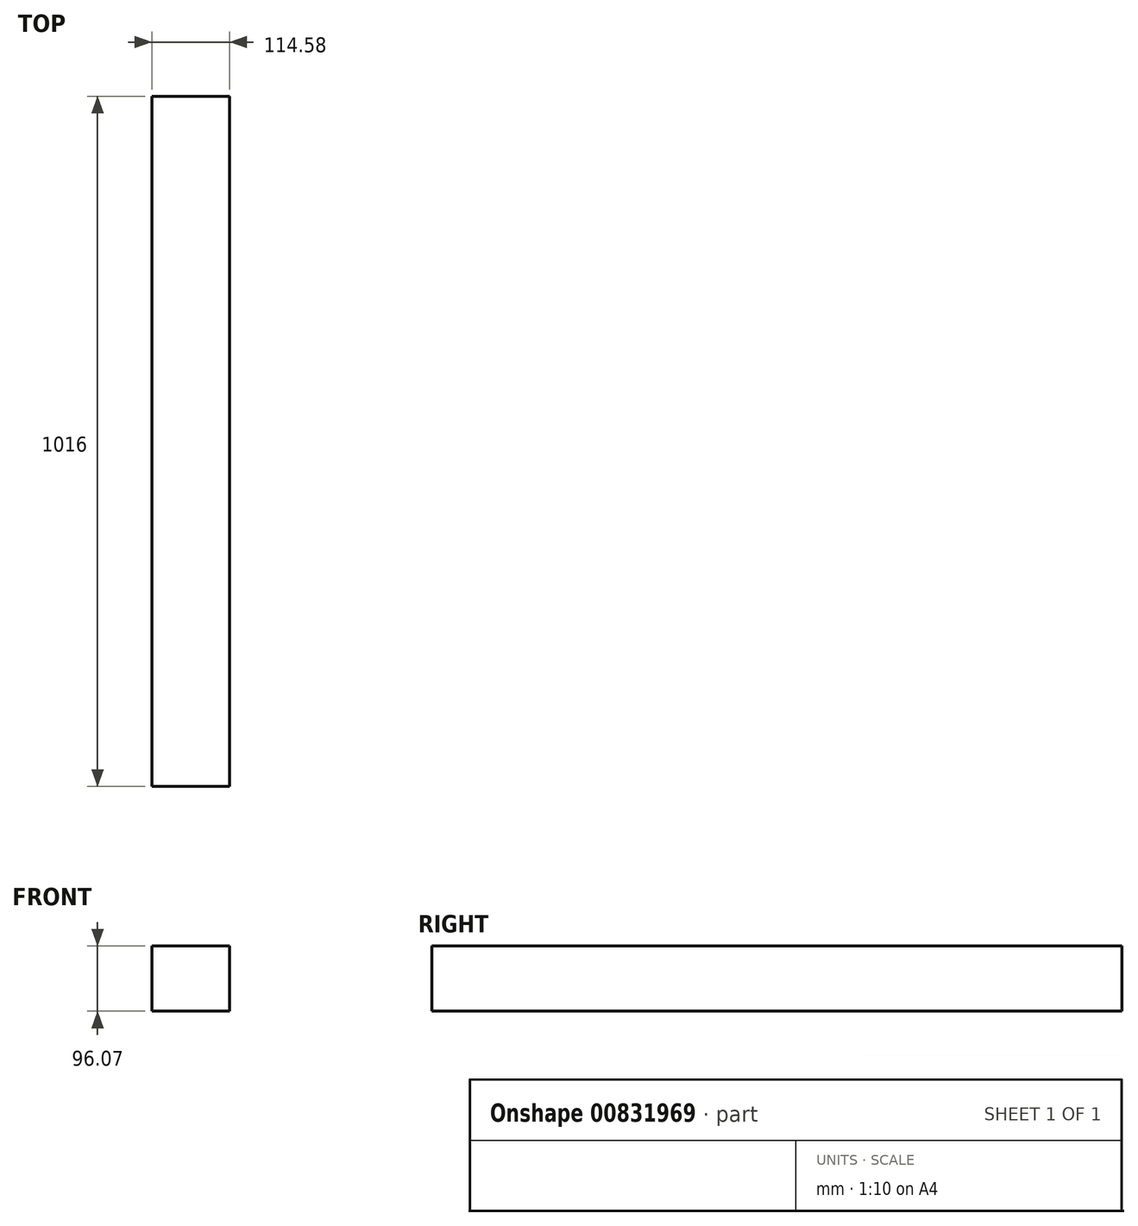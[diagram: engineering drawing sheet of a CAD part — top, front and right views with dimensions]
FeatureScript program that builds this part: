
annotation { "Feature Type Name" : "Feature", "Feature Type Description" : "" }
export const myFeature = defineFeature(function(context is Context, id is Id, definition is map)
    precondition{}
    {
        {
            var Q0;
            Q0=qCreatedBy(makeId("Front.planeOp"),FACE);
            var sketch = newSketch(context, id + "F0", { "sketchPlane" : qUnion([Q0])});
            skLineSegment(sketch, "E0.bottom", {"start": v(-55.12, 46.88) * mm, "end": v(59.46, 46.88) * mm});
            skLineSegment(sketch, "E0.top", {"start": v(-55.12, -49.2) * mm, "end": v(59.46, -49.2) * mm});
            skLineSegment(sketch, "E0.left", {"start": v(-55.12, 46.88) * mm, "end": v(-55.12, -49.2) * mm});
            skLineSegment(sketch, "E0.right", {"start": v(59.46, 46.88) * mm, "end": v(59.46, -49.2) * mm});
            skSolve(sketch);
        }
        {
            var Q0;
            Q0=makeQuery(id+"F0.imprint","IMPRINT",FACE,{"disambiguationData":[TD([[makeQuery(id+"F0.imprint","IMPRINT",EDGE,{"derivedFrom":sQuery(id+"F0.wireOp",EDGE,"E0.bottom")}),-1.0]])]});
            extrude(context, id + "F1", {"entities" : qUnion([Q0]), "depth" : 1016 * mm, "offsetDistance" : 25.4 * mm});
        }
    });
